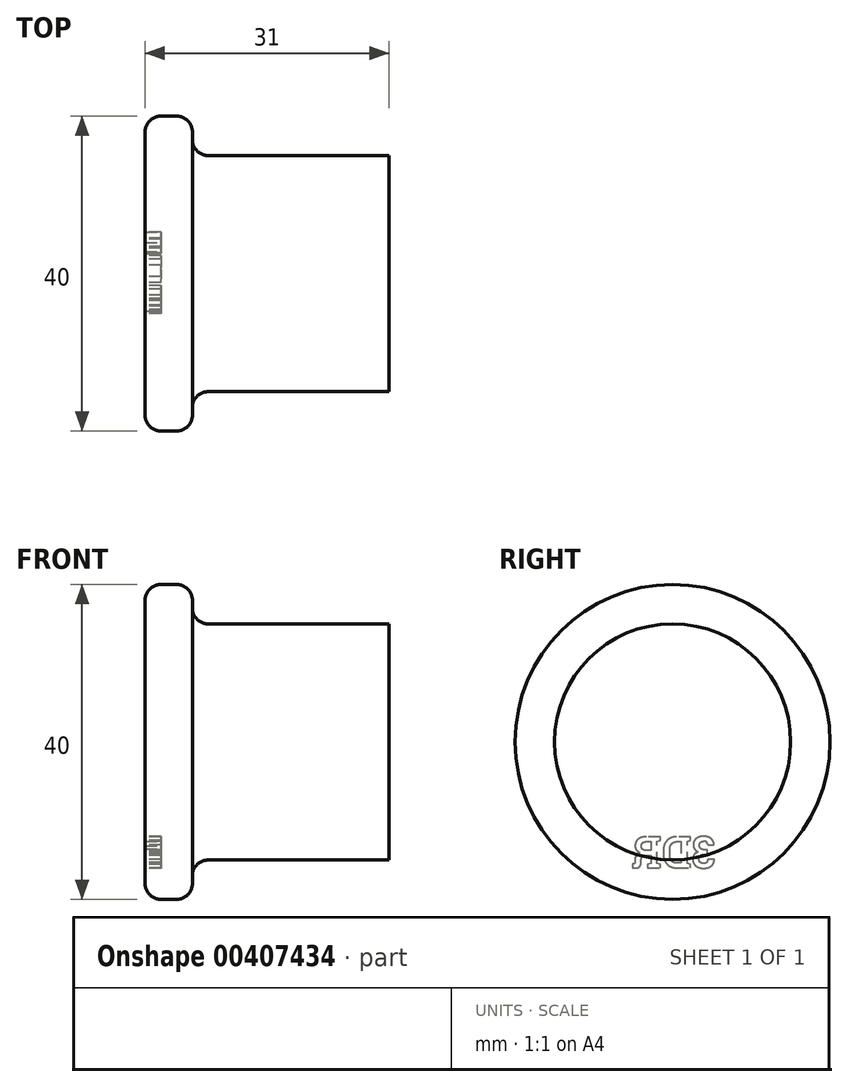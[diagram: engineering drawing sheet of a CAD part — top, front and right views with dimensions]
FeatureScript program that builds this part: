
annotation { "Feature Type Name" : "Feature", "Feature Type Description" : "" }
export const myFeature = defineFeature(function(context is Context, id is Id, definition is map)
    precondition{}
    {
        {
            var Q0;
            Q0=qCreatedBy(makeId("Front.planeOp"),FACE);
            var sketch = newSketch(context, id + "F0", { "sketchPlane" : qUnion([Q0])});
            skLineSegment(sketch, "E0", {"start": v(-31, 20) * mm, "end": v(-31, 0) * mm});
            skLineSegment(sketch, "E1", {"start": v(-31, 20) * mm, "end": v(-25, 20) * mm});
            skLineSegment(sketch, "E2", {"start": v(-25, 20) * mm, "end": v(-25, 15) * mm});
            skLineSegment(sketch, "E3", {"start": v(-25, 15) * mm, "end": v(0, 15) * mm});
            skLineSegment(sketch, "E4", {"start": v(0, 15) * mm, "end": v(0, 0) * mm});
            skLineSegment(sketch, "E5", {"start": v(0, 0) * mm, "end": v(-31, 0) * mm});
            skSolve(sketch);
        }
        {
            var Q0;
            Q0=makeQuery(id+"F0.imprint","IMPRINT",FACE,{"disambiguationData":[TD([[makeQuery(id+"F0.imprint","IMPRINT",EDGE,{"derivedFrom":sQuery(id+"F0.wireOp",EDGE,"E0")}),1.0]])]});
            var Q1;
            Q1=sQuery(id+"F0.wireOp",EDGE,"E5");
            revolve(context, id + "F1", {"entities" : qUnion([Q0]), "axis" : qUnion([Q1]), "revolveType" : RevolveType.FULL});
        }
        {
            var Q0;
            Q0=makeQuery(id+"F1.opRevolve","SWEPT_FACE",FACE,{"disambiguationData":[OSD([sQuery(id+"F0.wireOp",EDGE,"E4")])]});
            var sketch = newSketch(context, id + "F2", { "sketchPlane" : qUnion([Q0])});
            skCircle(sketch, "E6", {"center": v(0, 0) * mm, "radius": 5.25 * mm});
            skSolve(sketch);
        }
        {
            var Q0;
            Q0=makeQuery(id+"F1.opRevolve","SWEPT_FACE",FACE,{"disambiguationData":[OSD([sQuery(id+"F0.wireOp",EDGE,"E0")])]});
            var sketch = newSketch(context, id + "F3", { "sketchPlane" : qUnion([Q0])});
            skText(sketch, "E7", { "text": "3DR", "fontName": "RobotoSlab-Bold.ttf"});
            const initialGuessF3  = {"E7": [-0.00545, -0.016, 1, 0, 0.004]};
            skSetInitialGuess(sketch, initialGuessF3);
            skSolve(sketch);
        }
        {
            var Q0;
            Q0 = qSketchRegion(id + "F3", true);
            extrude(context, id + "F4", {"entities" : qUnion([Q0]), "operationType" : NewBodyOperationType.REMOVE, "oppositeDirection" : true, "depth" : 2 * mm});
        }
        {
            var Q0;
            Q0=makeQuery(id+"F1.opRevolve","SWEPT_EDGE",EDGE,{"disambiguationData":[OSD([sQuery(id+"F0.wireOp",EDGE,"E0"),sQuery(id+"F0.wireOp",EDGE,"E1")])]});
            var Q1;
            Q1=makeQuery(id+"F1.opRevolve","SWEPT_EDGE",EDGE,{"disambiguationData":[OSD([sQuery(id+"F0.wireOp",EDGE,"E2"),sQuery(id+"F0.wireOp",EDGE,"E3")])]});
            var Q2;
            Q2=makeQuery(id+"F1.opRevolve","SWEPT_EDGE",EDGE,{"disambiguationData":[OSD([sQuery(id+"F0.wireOp",EDGE,"E1"),sQuery(id+"F0.wireOp",EDGE,"E2")])]});
            fillet(context, id + "F5", {"entities" : qUnion([Q0, Q1, Q2]), "radius" : 2 * mm, "tangentPropagation" : true, "allowEdgeOverflow" : false});
        }
    });
